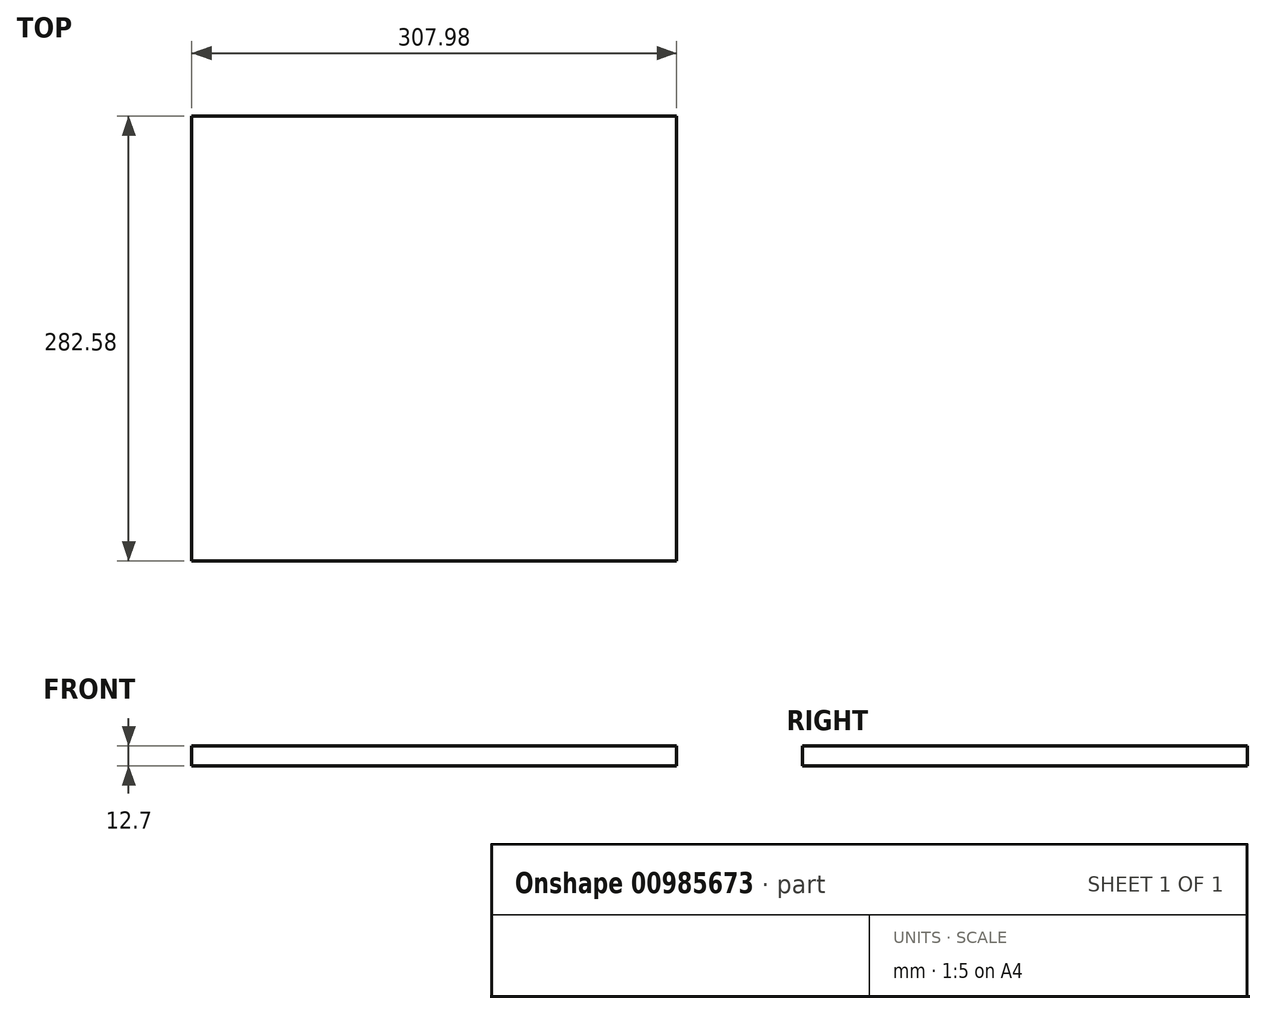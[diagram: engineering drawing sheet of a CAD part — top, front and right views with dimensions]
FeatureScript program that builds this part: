
annotation { "Feature Type Name" : "Feature", "Feature Type Description" : "" }
export const myFeature = defineFeature(function(context is Context, id is Id, definition is map)
    precondition{}
    {
        {
            var Q0;
            Q0=qCreatedBy(makeId("Top.planeOp"),FACE);
            var sketch = newSketch(context, id + "F0", { "sketchPlane" : qUnion([Q0])});
            skLineSegment(sketch, "E0.bottom", {"start": v(153.99, 141.29) * mm, "end": v(-153.99, 141.29) * mm});
            skLineSegment(sketch, "E0.top", {"start": v(153.99, -141.29) * mm, "end": v(-153.99, -141.29) * mm});
            skLineSegment(sketch, "E0.left", {"start": v(153.99, 141.29) * mm, "end": v(153.99, -141.29) * mm});
            skLineSegment(sketch, "E0.right", {"start": v(-153.99, 141.29) * mm, "end": v(-153.99, -141.29) * mm});
            skPoint(sketch, "E0.middle", {"position": v(0, 0) * mm});
            skSolve(sketch);
        }
        {
            var Q0;
            Q0 = qSketchRegion(id + "F0", true);
            extrude(context, id + "F1", {"entities" : qUnion([Q0]), "depth" : 12.7 * mm, "offsetDistance" : 25.4 * mm});
        }
    });
